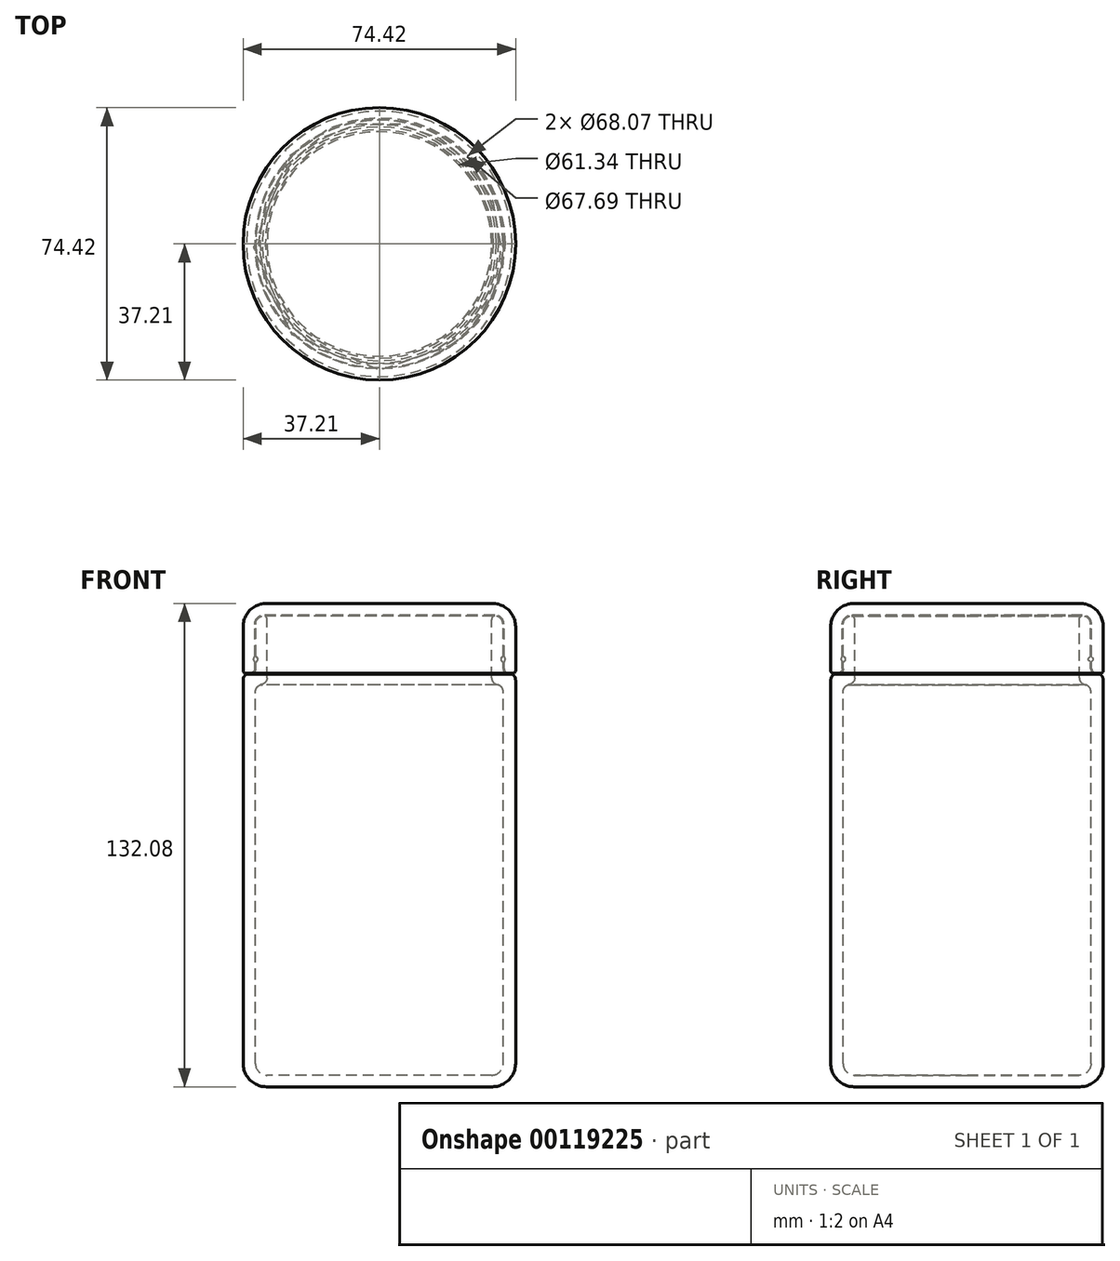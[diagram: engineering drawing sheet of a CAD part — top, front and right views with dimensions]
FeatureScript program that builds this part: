
annotation { "Feature Type Name" : "Feature", "Feature Type Description" : "" }
export const myFeature = defineFeature(function(context is Context, id is Id, definition is map)
    precondition{}
    {
        {
            var Q0;
            Q0=qCreatedBy(makeId("Front.planeOp"),FACE);
            var sketch = newSketch(context, id + "F0", { "sketchPlane" : qUnion([Q0])});
            skLineSegment(sketch, "E0", {"start": v(0, 0) * mm, "end": v(30.86, 0) * mm});
            skLineSegment(sketch, "E1", {"start": v(30.86, 132.08) * mm, "end": v(0, 132.08) * mm});
            skLineSegment(sketch, "E2", {"start": v(35.3, 113.03) * mm, "end": v(35.3, 113.03) * mm});
            skLineSegment(sketch, "E3", {"start": v(34.04, 114.3) * mm, "end": v(34.04, 116.08) * mm});
            skLineSegment(sketch, "E4", {"start": v(30.67, 127.64) * mm, "end": v(30.67, 111.76) * mm});
            skLineSegment(sketch, "E5", {"start": v(31.94, 109.86) * mm, "end": v(32.58, 109.86) * mm});
            skLineSegment(sketch, "E6", {"start": v(33.85, 107.95) * mm, "end": v(33.85, 6.35) * mm});
            skLineSegment(sketch, "E7", {"start": v(30.67, 3.18) * mm, "end": v(0, 3.17) * mm});
            skPoint(sketch, "E8.visualSharp", {"position": v(33.85, 109.86) * mm});
            skArc(sketch, "E8.filletArc", {"start": v(33.85, 107.95) * mm, "mid": v(33.29, 109.3) * mm, "end": v(31.94, 109.86) * mm});
            skPoint(sketch, "E9.visualSharp", {"position": v(30.67, 109.86) * mm});
            skArc(sketch, "E9.filletArc", {"start": v(30.67, 111.76) * mm, "mid": v(31.23, 110.41) * mm, "end": v(32.58, 109.86) * mm});
            skPoint(sketch, "E10.visualSharp", {"position": v(34.04, 113.03) * mm});
            skArc(sketch, "E10.filletArc", {"start": v(34.04, 114.3) * mm, "mid": v(34.4, 113.4) * mm, "end": v(35.3, 113.03) * mm});
            skLineSegment(sketch, "E11", {"start": v(37.21, 125.73) * mm, "end": v(37.21, 113.67) * mm});
            skLineSegment(sketch, "E12", {"start": v(37.21, 6.35) * mm, "end": v(37.21, 111.13) * mm});
            skPoint(sketch, "E13.visualSharp", {"position": v(37.21, 113.03) * mm});
            skArc(sketch, "E13.filletArc", {"start": v(37.21, 111.13) * mm, "mid": v(36.96, 112.08) * mm, "end": v(36.26, 112.78) * mm});
            skLineSegment(sketch, "E14", {"start": v(36.58, 113.03) * mm, "end": v(35.3, 113.03) * mm});
            skArc(sketch, "E15.filletArc", {"start": v(36.58, 113.03) * mm, "mid": v(37.03, 113.22) * mm, "end": v(37.21, 113.67) * mm});
            skPoint(sketch, "E16.visualSharp", {"position": v(34.04, 128.9) * mm});
            skLineSegment(sketch, "E17", {"start": v(31.94, 128.9) * mm, "end": v(31.5, 128.9) * mm});
            skLineSegment(sketch, "E18", {"start": v(30.67, 128.9) * mm, "end": v(0, 128.9) * mm});
            skPoint(sketch, "E19.visualSharp", {"position": v(30.67, 128.9) * mm});
            skArc(sketch, "E19.filletArc", {"start": v(31.18, 128.65) * mm, "mid": v(30.8, 128.2) * mm, "end": v(30.67, 127.64) * mm});
            skArc(sketch, "E20.filletArc", {"start": v(34.04, 126.37) * mm, "mid": v(33.3, 128.16) * mm, "end": v(31.5, 128.9) * mm});
            skLineSegment(sketch, "E21", {"start": v(30.67, 128.9) * mm, "end": v(31.5, 128.9) * mm});
            skLineSegment(sketch, "E22.0", {"start": v(33.78, 114.3) * mm, "end": v(33.78, 115.94) * mm});
            skArc(sketch, "E23.0", {"start": v(33.78, 114.3) * mm, "mid": v(34.23, 113.22) * mm, "end": v(35.3, 112.78) * mm});
            skLineSegment(sketch, "E24", {"start": v(35.3, 112.78) * mm, "end": v(36.26, 112.78) * mm});
            skArc(sketch, "E25.0", {"start": v(33.78, 126.37) * mm, "mid": v(33.11, 127.98) * mm, "end": v(31.5, 128.65) * mm});
            skLineSegment(sketch, "E26", {"start": v(31.5, 128.65) * mm, "end": v(31.18, 128.65) * mm});
            skLineSegment(sketch, "E27", {"start": v(0, 132.08) * mm, "end": v(0, 128.9) * mm});
            skLineSegment(sketch, "E28", {"start": v(0, 3.17) * mm, "end": v(0, 0) * mm});
            skArc(sketch, "E29", {"start": v(33.57, 117.44) * mm, "mid": v(33.15, 116.84) * mm, "end": v(33.57, 116.24) * mm});
            skLineSegment(sketch, "E30.trimOffspring", {"start": v(33.78, 117.74) * mm, "end": v(33.78, 127.64) * mm});
            skPoint(sketch, "E31.visualSharp", {"position": v(33.78, 116.2) * mm});
            skArc(sketch, "E31.filletArc", {"start": v(33.78, 115.94) * mm, "mid": v(33.72, 116.13) * mm, "end": v(33.57, 116.24) * mm});
            skPoint(sketch, "E32.visualSharp", {"position": v(33.78, 117.48) * mm});
            skArc(sketch, "E32.filletArc", {"start": v(33.57, 117.44) * mm, "mid": v(33.72, 117.55) * mm, "end": v(33.78, 117.74) * mm});
            skPoint(sketch, "E33.visualSharp", {"position": v(37.21, 132.08) * mm});
            skArc(sketch, "E33.filletArc", {"start": v(37.21, 125.73) * mm, "mid": v(35.35, 130.22) * mm, "end": v(30.86, 132.08) * mm});
            skArc(sketch, "E34", {"start": v(34.16, 116.33) * mm, "mid": v(34.42, 116.84) * mm, "end": v(34.16, 117.35) * mm});
            skLineSegment(sketch, "E35.trimOffspring", {"start": v(34.04, 117.6) * mm, "end": v(34.04, 126.37) * mm});
            skPoint(sketch, "E36.visualSharp", {"position": v(34.04, 116.26) * mm});
            skArc(sketch, "E36.filletArc", {"start": v(34.16, 116.33) * mm, "mid": v(34.07, 116.22) * mm, "end": v(34.04, 116.08) * mm});
            skPoint(sketch, "E37.visualSharp", {"position": v(34.04, 117.42) * mm});
            skArc(sketch, "E37.filletArc", {"start": v(34.04, 117.6) * mm, "mid": v(34.07, 117.46) * mm, "end": v(34.16, 117.35) * mm});
            skPoint(sketch, "E38.visualSharp", {"position": v(33.85, 3.18) * mm});
            skArc(sketch, "E38.filletArc", {"start": v(30.67, 3.18) * mm, "mid": v(32.92, 4.1) * mm, "end": v(33.85, 6.35) * mm});
            skPoint(sketch, "E39.visualSharp", {"position": v(37.21, 0) * mm});
            skArc(sketch, "E39.filletArc", {"start": v(30.86, 0) * mm, "mid": v(35.35, 1.86) * mm, "end": v(37.21, 6.35) * mm});
            skSolve(sketch);
        }
        {
            var Q0;
            Q0=makeQuery(id+"F0.imprint","IMPRINT",FACE,{"disambiguationData":[TD([[makeQuery(id+"F0.imprint","IMPRINT",EDGE,{"derivedFrom":sQuery(id+"F0.wireOp",EDGE,"E1")}),1.0]])]});
            var Q1;
            Q1=sQuery(id+"F0.wireOp",EDGE,"E27");
            revolve(context, id + "F1", {"entities" : qUnion([Q0]), "axis" : qUnion([Q1]), "revolveType" : RevolveType.FULL});
        }
        {
            var Q0;
            Q0=makeQuery(id+"F0.imprint","IMPRINT",FACE,{"disambiguationData":[TD([[makeQuery(id+"F0.imprint","IMPRINT",EDGE,{"derivedFrom":sQuery(id+"F0.wireOp",EDGE,"E0")}),1.0]])]});
            var Q1;
            Q1=sQuery(id+"F0.wireOp",EDGE,"E28");
            revolve(context, id + "F2", {"entities" : qUnion([Q0]), "axis" : qUnion([Q1]), "revolveType" : RevolveType.FULL});
        }
    });
